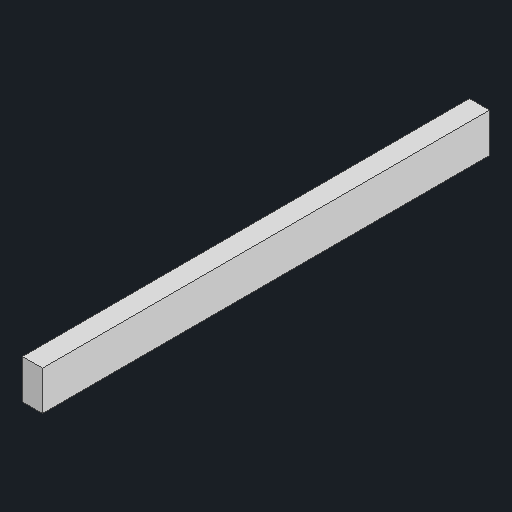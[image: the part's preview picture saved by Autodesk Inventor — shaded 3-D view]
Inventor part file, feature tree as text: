
AUTODESK INVENTOR PART (.ipt)
format: ipt  version: 2022 (Build 260153000, 153)  size: 219,648 bytes
history: native  units: in
note: dims shown in document units (in); Inventor stores cm internally (conversion verified against a paired STEP export)
features: reference x4, other x3, extrude x1, sketch x1
ambient origin geometry x8: Origin, YZ Plane, XZ Plane, XY Plane, X Axis, Y Axis, Z Axis, Center Point
bodies: Solid1 (feature_tree)
feature tree (9):
  extrude  "Extrusion1"  Depth=2.0in TaperAngle=0.0deg
  sketch  "Sketch1"  dims[d0=0.005in d1=2.0in d2=0.0in]
  reference  "Reference1"
  reference  "Reference2"
  reference  "Reference3"
  reference  "Reference4"
  parser-record x1  (decoder bookkeeping rows leaked as tree rows — omitted from the tree; the rows remain in map.json)
  other  "Prototype Assembly.iam"
  other  "Vertical Beam Prototype:1"
note: 1 file-system path scrubbed to <path> (originals preserved in map.json)
